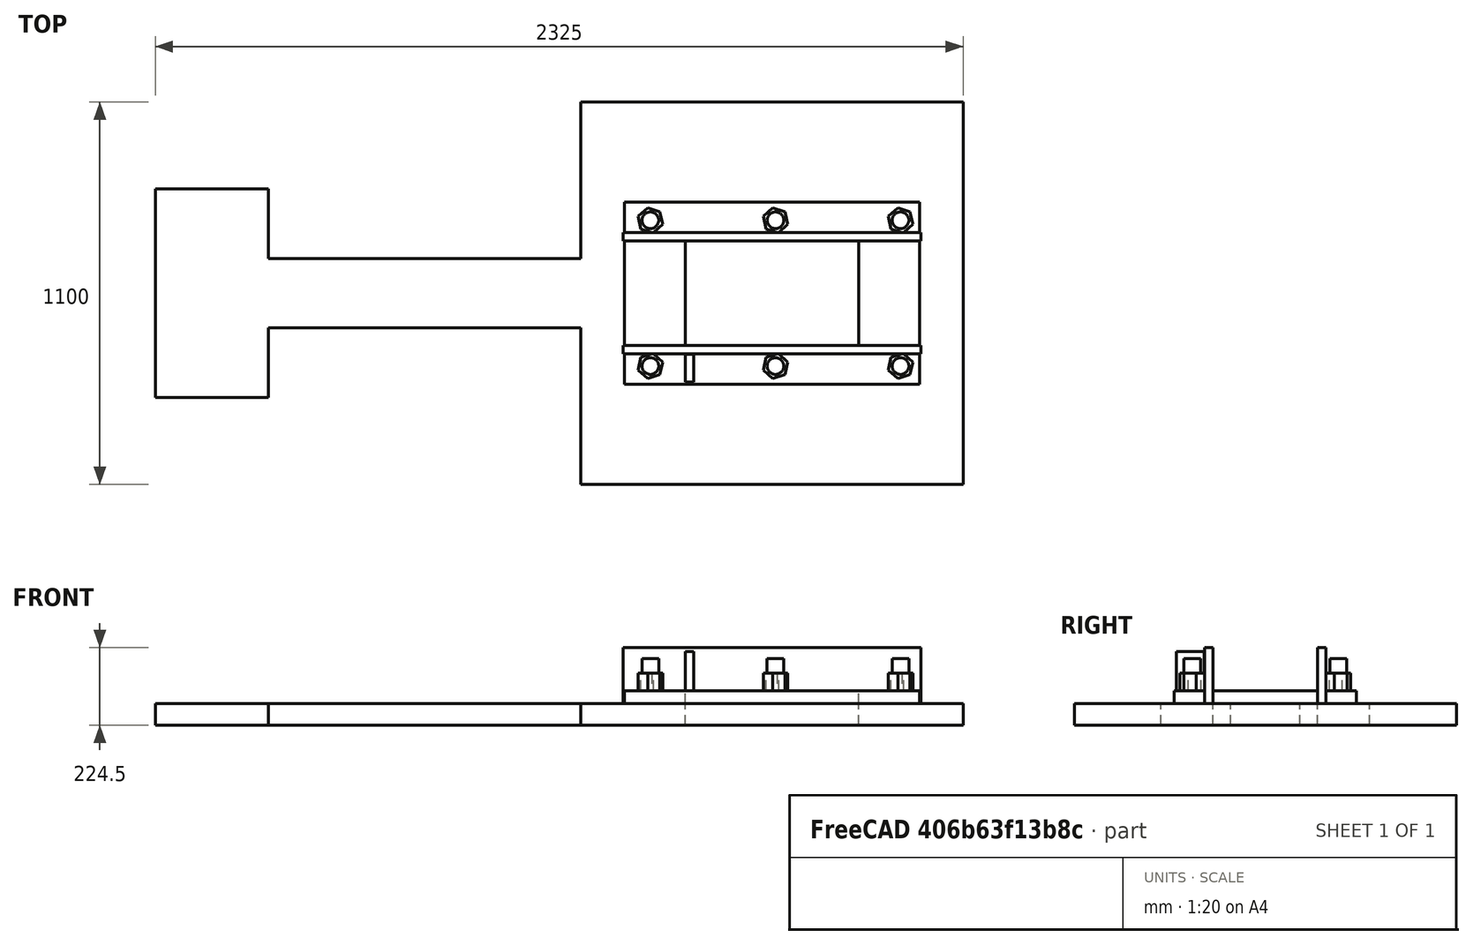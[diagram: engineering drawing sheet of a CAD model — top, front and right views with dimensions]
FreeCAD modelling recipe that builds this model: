
FCSTD DOCUMENT  (FreeCAD 0.17R5235 (Git shallow))
Label: BaseMatLourd
License: All rights reserved
LicenseURL: http://en.wikipedia.org/wiki/All_rights_reserved
objects: Sketcher::SketchObject×7, PartDesign::Pad×6, PartDesign::Mirrored×3, PartDesign::LinearPattern×2, PartDesign::MultiTransform×2, PartDesign::Body×1, PartDesign::Chamfer×1, PartDesign::Pocket×1
note: 30 computed .brp shape members not serialized (recipe doc carries the construction recipe); baked Part::Feature solids carry a one-line shape summary decoded from their .brp

FEATURE [Sketcher::SketchObject] Sketch  label="Massif_Sketch"
  MapMode = 5
  Support = -> [XY_Plane]
  sketch-geometry (12):
    g0: LineSegment StartX=-550 StartY=550 StartZ=0 EndX=550 EndY=550 EndZ=0
    g1: LineSegment StartX=550 StartY=550 StartZ=0 EndX=550 EndY=-550 EndZ=0
    g2: LineSegment StartX=550 StartY=-550 StartZ=0 EndX=-550 EndY=-550 EndZ=0
    g3: LineSegment StartX=-1775 StartY=300 StartZ=0 EndX=-1450 EndY=300 EndZ=0
    g4: LineSegment StartX=-1450 StartY=-300 StartZ=0 EndX=-1775 EndY=-300 EndZ=0
    g5: LineSegment StartX=-1775 StartY=-300 StartZ=0 EndX=-1775 EndY=300 EndZ=0
    g6: LineSegment StartX=-1450 StartY=100 StartZ=0 EndX=-550 EndY=100 EndZ=0
    g7: LineSegment StartX=-1450 StartY=-100 StartZ=0 EndX=-550 EndY=-100 EndZ=0
    g8: LineSegment StartX=-550 StartY=550 StartZ=0 EndX=-550 EndY=100 EndZ=0
    g9: LineSegment StartX=-550 StartY=-100 StartZ=0 EndX=-550 EndY=-550 EndZ=0
    g10: LineSegment StartX=-1450 StartY=300 StartZ=0 EndX=-1450 EndY=100 EndZ=0
    g11: LineSegment StartX=-1450 StartY=-100 StartZ=0 EndX=-1450 EndY=-300 EndZ=0
  constraints (33):
    c: Coincident(g0,g1)
    c: Coincident(g1,g2)
    c: Horizontal(g0)
    c: Horizontal(g2)
    c: Vertical(g1)
    c: DistanceX(g0,g0) = 1100
    c: DistanceY(g1,g0) = 1100
    c: Coincident(g4,g5)
    c: Coincident(g5,g3)
    c: Horizontal(g3)
    c: Horizontal(g4)
    c: Vertical(g5)
    c: Horizontal(g6)
    c: Horizontal(g7)
    c: DistanceY(g7,g6) = 200
    c: DistanceY(g4,g3) = 600
    c: DistanceX(g3,g3) = 325
    c: Symmetric(g4,g3,g-1)
    c: Symmetric(g6,g7,g-1)
    c: Symmetric(g0,g0,g-2)
    c: DistanceX(g6,g6) = 900
    c: Coincident(g8,g0)
    c: Coincident(g8,g6)
    c: Vertical(g8)
    c: Coincident(g9,g7)
    c: Coincident(g9,g2)
    c: Vertical(g9)
    c: Coincident(g10,g6)
    c: Vertical(g10)
    c: Coincident(g11,g7)
    c: Coincident(g11,g4)
    c: Vertical(g11)
    c: Coincident(g10,g3)
FEATURE [PartDesign::Mirrored] Mirrored001  label="Equerre_Mirrored"
  MirrorPlane = -> XZ_Plane
FEATURE [PartDesign::Mirrored] Mirrored002  label="Boulon_Mirrored"
  MirrorPlane = -> XZ_Plane
FEATURE [PartDesign::Pad] Pad  label="Massif_Pad"
  Length = 62.5
  Length2 = 100
  Profile = -> Sketch
  Type = 0
FEATURE [Sketcher::SketchObject] Sketch001  label="Socle_Sketch"
  MapMode = 5
  Placement = pos=(0,0,62.5) rot=(0,0,1;0rad)
  Support = -> [Pad]
  sketch-geometry (4):
    g0: LineSegment StartX=-425 StartY=262.5 StartZ=0 EndX=425 EndY=262.5 EndZ=0
    g1: LineSegment StartX=425 StartY=262.5 StartZ=0 EndX=425 EndY=-262.5 EndZ=0
    g2: LineSegment StartX=425 StartY=-262.5 StartZ=0 EndX=-425 EndY=-262.5 EndZ=0
    g3: LineSegment StartX=-425 StartY=-262.5 StartZ=0 EndX=-425 EndY=262.5 EndZ=0
  constraints (12):
    c: Coincident(g0,g1)
    c: Coincident(g1,g2)
    c: Coincident(g2,g3)
    c: Coincident(g3,g0)
    c: Horizontal(g0)
    c: Horizontal(g2)
    c: Vertical(g1)
    c: Vertical(g3)
    c: DistanceY(g1,g0) = 525
    c: DistanceX(g0,g0) = 850
    c: Symmetric(g0,g2,g-1)
    c: Symmetric(g0,g0,g-2)
FEATURE [PartDesign::Pad] Pad001  label="Socle_Pad"
  BaseFeature = -> Pad
  Length = 37.5
  Length2 = 100
  Profile = -> Sketch001
  Type = 0
FEATURE [Sketcher::SketchObject] Sketch002  label="Support_Sketch"
  MapMode = 5
  Placement = pos=(0,0,62.5) rot=(0,0,1;0rad)
  Support = -> [Pad001]
  sketch-geometry (4):
    g0: LineSegment StartX=-428.345 StartY=-150 StartZ=0 EndX=428.345 EndY=-150 EndZ=0
    g1: LineSegment StartX=428.345 StartY=-150 StartZ=0 EndX=428.345 EndY=-175 EndZ=0
    g2: LineSegment StartX=428.345 StartY=-175 StartZ=0 EndX=-428.345 EndY=-175 EndZ=0
    g3: LineSegment StartX=-428.345 StartY=-175 StartZ=0 EndX=-428.345 EndY=-150 EndZ=0
  constraints (11):
    c: Coincident(g0,g1)
    c: Coincident(g1,g2)
    c: Coincident(g2,g3)
    c: Coincident(g3,g0)
    c: Horizontal(g0)
    c: Horizontal(g2)
    c: Vertical(g1)
    c: Vertical(g3)
    c: DistanceY(g1,g0) = 25
    c: DistanceY(g0,g-1) = 150
    c: Symmetric(g0,g0,g-2)
FEATURE [Sketcher::SketchObject] Sketch005  label="Ecrou_Sketch"
  MapMode = 5
  Placement = pos=(0,0,100) rot=(0,0,1;0rad)
  Support = -> [Pad001]
  sketch-geometry (7):
    g0: LineSegment StartX=-314.751 StartY=-198.751 StartZ=0 EndX=-342.117 EndY=-173.849 EndZ=0
    g1: LineSegment StartX=-342.117 StartY=-173.849 StartZ=0 EndX=-377.366 EndY=-185.098 EndZ=0
    g2: LineSegment StartX=-377.366 StartY=-185.098 StartZ=0 EndX=-385.249 EndY=-221.249 EndZ=0
    g3: LineSegment StartX=-385.249 StartY=-221.249 StartZ=0 EndX=-357.883 EndY=-246.151 EndZ=0
    g4: LineSegment StartX=-357.883 StartY=-246.151 StartZ=0 EndX=-322.634 EndY=-234.902 EndZ=0
    g5: LineSegment StartX=-322.634 StartY=-234.902 StartZ=0 EndX=-314.751 EndY=-198.751 EndZ=0
    g6: Circle [constr] CenterX=-350 CenterY=-210 CenterZ=0 NormalX=0 NormalY=0 NormalZ=1 AngleXU=0 Radius=37
  constraints (16):
    c: Coincident(g0,g1)
    c: Coincident(g1,g2)
    c: Coincident(g2,g3)
    c: Coincident(g3,g4)
    c: Coincident(g4,g5)
    c: Coincident(g5,g0)
    c: Equal(g0, g1-g5) x5
    c: PointOnObject(g0,g6)
    c: PointOnObject(g1,g6)
    c: PointOnObject(g2,g6)
    c: PointOnObject(g3,g6)
    c: PointOnObject(g4,g6)
    c: PointOnObject(g5,g6)
    c: Radius(g6) = 37
    c: DistanceX(g6,g-1) = 350
    c: DistanceY(g6,g-1) = 210
FEATURE [PartDesign::LinearPattern] LinearPattern001  label="Boulon_LinearPattern"
  Direction = -> Sketch005 [H_Axis]
  Length = 720
  Occurrences = 3
FEATURE [PartDesign::Body] Body
  Group = -> [Sketch,Pad,Sketch001,Pad001,Pocket,Sketch002,Pad002,Mirrored,Sketch003,Sketch004,Pad003,MultiTransform,LinearPattern,Mirrored001,Sketch005,Pad004,Sketch006,Pad005,MultiTransform001,LinearPattern001,Mirrored002]
  Origin = -> Origin
  Tip = -> MultiTransform001
FEATURE [PartDesign::Pad] Pad002  label="Support_Pad"
  BaseFeature = -> Pocket
  Length = 162
  Length2 = 100
  Profile = -> Sketch002
  Type = 0
FEATURE [PartDesign::Chamfer] Chamfer  label="Support_Chamfer"
  Base = -> MultiTransform001 [Edge137,Edge139,Edge96,Edge114,Edge342,Edge334,Edge326,Edge350,Edge300,Edge276,Edge284,Edge292]
  BaseFeature = -> MultiTransform001
  Size = 78
FEATURE [PartDesign::Mirrored] Mirrored  label="Support_Mirrored"
  BaseFeature = -> Pad002
  MirrorPlane = -> XZ_Plane
  Originals = -> [Pad002]
FEATURE [Sketcher::SketchObject] Sketch003  label="Trou_Mat_Sketch"
  MapMode = 5
  Placement = pos=(0,-3.1e-11,150) rot=(0,0,1;0rad)
  Support = -> [Chamfer]
  sketch-geometry (4):
    g0: LineSegment StartX=-250 StartY=150 StartZ=0 EndX=250 EndY=150 EndZ=0
    g1: LineSegment StartX=250 StartY=150 StartZ=0 EndX=250 EndY=-150 EndZ=0
    g2: LineSegment StartX=250 StartY=-150 StartZ=0 EndX=-250 EndY=-150 EndZ=0
    g3: LineSegment StartX=-250 StartY=-150 StartZ=0 EndX=-250 EndY=150 EndZ=0
  constraints (12):
    c: Coincident(g0,g1)
    c: Coincident(g1,g2)
    c: Coincident(g2,g3)
    c: Coincident(g3,g0)
    c: Horizontal(g0)
    c: Horizontal(g2)
    c: Vertical(g1)
    c: Vertical(g3)
    c: DistanceY(g1,g0) = 300
    c: DistanceX(g2,g1) = 500
    c: Symmetric(g2,g0,g-1)
    c: Symmetric(g0,g0,g-2)
FEATURE [PartDesign::Pocket] Pocket  label="Trou_Mat_Pocket"
  BaseFeature = -> Pad001
  Length = 100
  Length2 = 100
  Profile = -> Sketch003
  Type = 0
FEATURE [Sketcher::SketchObject] Sketch004  label="Equerre_Sketch"
  MapMode = 5
  Placement = pos=(-550,0,0) rot=(0.57735,-0.57735,-0.57735;2.0944rad)
  Support = -> [Chamfer]
  sketch-geometry (4):
    g0: LineSegment StartX=-250 StartY=-175.948 StartZ=0 EndX=-225 EndY=-175.948 EndZ=0
    g1: LineSegment StartX=-225 StartY=-175.948 StartZ=0 EndX=-225 EndY=-255.948 EndZ=0
    g2: LineSegment StartX=-225 StartY=-255.948 StartZ=0 EndX=-250 EndY=-255.948 EndZ=0
    g3: LineSegment StartX=-250 StartY=-255.948 StartZ=0 EndX=-250 EndY=-175.948 EndZ=0
  constraints (11):
    c: Coincident(g0,g1)
    c: Coincident(g1,g2)
    c: Coincident(g2,g3)
    c: Coincident(g3,g0)
    c: Horizontal(g0)
    c: Horizontal(g2)
    c: Vertical(g1)
    c: Vertical(g3)
    c: DistanceX(g2,g1) = 25
    c: DistanceY(g1,g0) = 80
    c: DistanceX(g0,g-1) = 250
FEATURE [PartDesign::Pad] Pad003  label="Equerre_Pad"
  BaseFeature = -> Mirrored
  Length = 112
  Length2 = 100
  Profile = -> Sketch004
  Type = 0
FEATURE [PartDesign::MultiTransform] MultiTransform  label="Equerre_MultiTransform"
  BaseFeature = -> Pad003
  Originals = -> [Pad003]
  Transformations = -> [LinearPattern,Mirrored001]
FEATURE [PartDesign::LinearPattern] LinearPattern  label="Equerre_LinearPattern"
  Direction = -> Sketch004 [H_Axis]
  Length = 500
  Occurrences = 4
FEATURE [PartDesign::Pad] Pad004  label="Ecrou_Pad"
  BaseFeature = -> MultiTransform
  Length = 50
  Length2 = 100
  Profile = -> Sketch005
  Type = 0
FEATURE [Sketcher::SketchObject] Sketch006  label="filletage_Sketch"
  MapMode = 5
  Placement = pos=(0,0,62.5) rot=(0,0,1;0rad)
  Support = -> [Pad004]
  sketch-geometry (1):
    g0: Circle CenterX=-350 CenterY=-210 CenterZ=0 NormalX=0 NormalY=0 NormalZ=1 AngleXU=0 Radius=24
  constraints (3):
    c: Radius(g0) = 24
    c: DistanceX(g0,g-1) = 350
    c: DistanceY(g0,g-1) = 210
FEATURE [PartDesign::Pad] Pad005  label="filletage_Pad"
  BaseFeature = -> Pad004
  Length = 130
  Length2 = 100
  Profile = -> Sketch006
  Type = 0
FEATURE [PartDesign::MultiTransform] MultiTransform001  label="Boulon_MultiTransform"
  BaseFeature = -> Pad005
  Originals = -> [Pad004,Pad005]
  Transformations = -> [LinearPattern001,Mirrored002]
